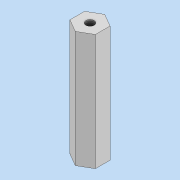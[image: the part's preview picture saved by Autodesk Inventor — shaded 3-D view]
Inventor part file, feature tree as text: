
AUTODESK INVENTOR PART (.ipt)
format: ipt  version: 2022 (Build 260153000, 153)  size: 88,064 bytes
history: native  units: in
note: dims shown in document units (in); Inventor stores cm internally (conversion verified against a paired STEP export)
features: sketch x3, hole x2, extrude x1
ambient origin geometry x8: Origin, YZ Plane, XZ Plane, XY Plane, X Axis, Y Axis, Z Axis, Center Point
bodies: Solid1 (feature_tree)
feature tree (6):
  extrude  "Extrusion1"  Depth=2.2835in TaperAngle=0.0deg
  hole  "Hole1"  [1 undecoded]
  hole  "Hole2"  [1 undecoded]
  sketch  "Sketch1"  dims[d0=0.25in d1=2.2835in d2=0.0in]
  sketch  "Sketch3"  dims[d3=0.1628in d4=0.3937in d5=0.1575in d6=0.0787in d7=90.0deg d8=0.5118in d9=0.8108in]
  sketch  "Sketch4"  dims[d10=0.1628in d11=0.5118in d12=0.1575in d13=0.0787in d14=90.0deg d15=0.5118in d16=0.8108in]
note: 2 required parameter values undecoded (feature->parameter linkage not recoverable at this tier; creation-order binding heuristic only, values carry confidence <= 0.55)
